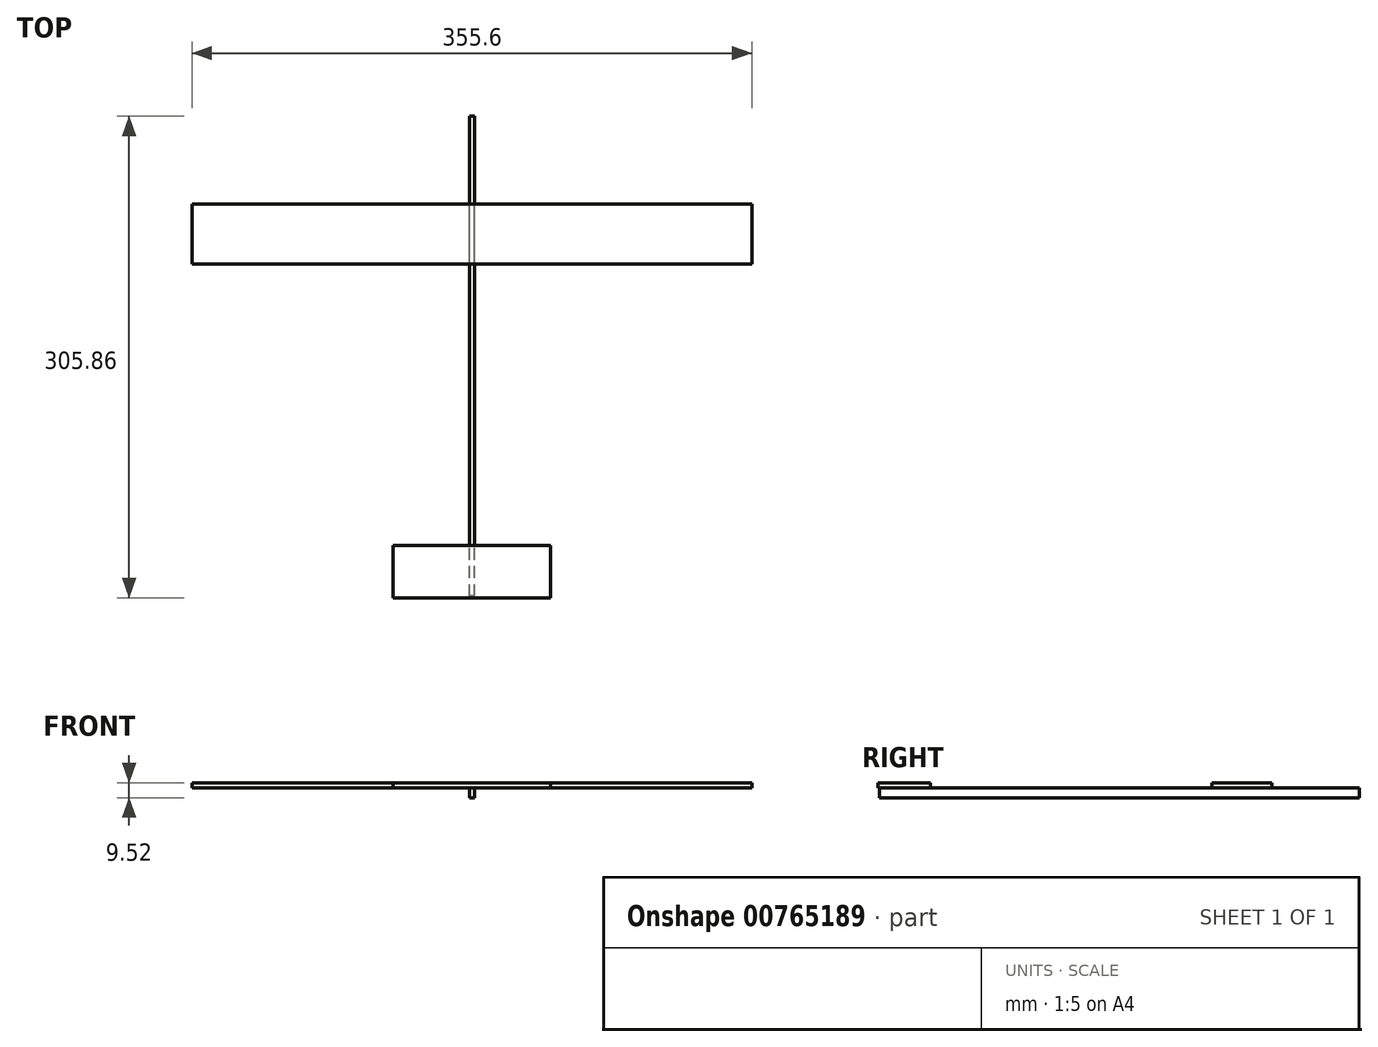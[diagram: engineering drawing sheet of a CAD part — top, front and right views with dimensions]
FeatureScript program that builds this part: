
annotation { "Feature Type Name" : "Feature", "Feature Type Description" : "" }
export const myFeature = defineFeature(function(context is Context, id is Id, definition is map)
    precondition{}
    {
        {
            var Q0;
            Q0=qCreatedBy(makeId("Top.planeOp"),FACE);
            var sketch = newSketch(context, id + "F0", { "sketchPlane" : qUnion([Q0])});
            skLineSegment(sketch, "E0.bottom", {"start": v(1.59, -152.4) * mm, "end": v(-1.59, -152.4) * mm});
            skLineSegment(sketch, "E0.top", {"start": v(1.59, 152.4) * mm, "end": v(-1.59, 152.4) * mm});
            skLineSegment(sketch, "E0.left", {"start": v(1.59, -152.4) * mm, "end": v(1.59, 152.4) * mm});
            skLineSegment(sketch, "E0.right", {"start": v(-1.59, -152.4) * mm, "end": v(-1.59, 152.4) * mm});
            skPoint(sketch, "E0.middle", {"position": v(0, 0) * mm});
            skSolve(sketch);
        }
        {
            var Q0;
            Q0=qCreatedBy(makeId("Top.planeOp"),FACE);
            var sketch = newSketch(context, id + "F1", { "sketchPlane" : qUnion([Q0])});
            skLineSegment(sketch, "E1.bottom", {"start": v(50, -153.46) * mm, "end": v(-50, -153.46) * mm});
            skLineSegment(sketch, "E1.top", {"start": v(50, -120.13) * mm, "end": v(-50, -120.13) * mm});
            skLineSegment(sketch, "E1.left", {"start": v(50, -153.46) * mm, "end": v(50, -120.13) * mm});
            skLineSegment(sketch, "E1.right", {"start": v(-50, -153.46) * mm, "end": v(-50, -120.13) * mm});
            skPoint(sketch, "E1.middle", {"position": v(0, -136.8) * mm});
            skLineSegment(sketch, "E2.bottom", {"start": v(177.8, 58.63) * mm, "end": v(-177.8, 58.63) * mm});
            skLineSegment(sketch, "E2.top", {"start": v(177.8, 96.73) * mm, "end": v(-177.8, 96.73) * mm});
            skLineSegment(sketch, "E2.left", {"start": v(177.8, 58.63) * mm, "end": v(177.8, 96.73) * mm});
            skLineSegment(sketch, "E2.right", {"start": v(-177.8, 58.63) * mm, "end": v(-177.8, 96.73) * mm});
            skPoint(sketch, "E2.middle", {"position": v(0, 77.68) * mm});
            skSolve(sketch);
        }
        {
            var Q0;
            Q0=makeQuery(id+"F1.imprint","IMPRINT",FACE,{"disambiguationData":[TD([[makeQuery(id+"F1.imprint","IMPRINT",EDGE,{"derivedFrom":sQuery(id+"F1.wireOp",EDGE,"E2.bottom")}),-1.0]])]});
            extrude(context, id + "F2", {"entities" : qUnion([Q0]), "depth" : 3.17 * mm, "offsetDistance" : 25.4 * mm});
        }
        {
            var Q0;
            Q0=makeQuery(id+"F1.imprint","IMPRINT",FACE,{"disambiguationData":[TD([[makeQuery(id+"F1.imprint","IMPRINT",EDGE,{"derivedFrom":sQuery(id+"F1.wireOp",EDGE,"E1.bottom")}),-1.0]])]});
            extrude(context, id + "F3", {"entities" : qUnion([Q0]), "depth" : 3.17 * mm, "offsetDistance" : 25.4 * mm});
        }
        {
            var Q0;
            Q0=makeQuery(id+"F0.imprint","IMPRINT",FACE,{"disambiguationData":[TD([[makeQuery(id+"F0.imprint","IMPRINT",EDGE,{"derivedFrom":sQuery(id+"F0.wireOp",EDGE,"E0.bottom")}),-1.0]])]});
            extrude(context, id + "F4", {"entities" : qUnion([Q0]), "depth" : -6.35 * mm, "offsetDistance" : 25.4 * mm});
        }
    });
